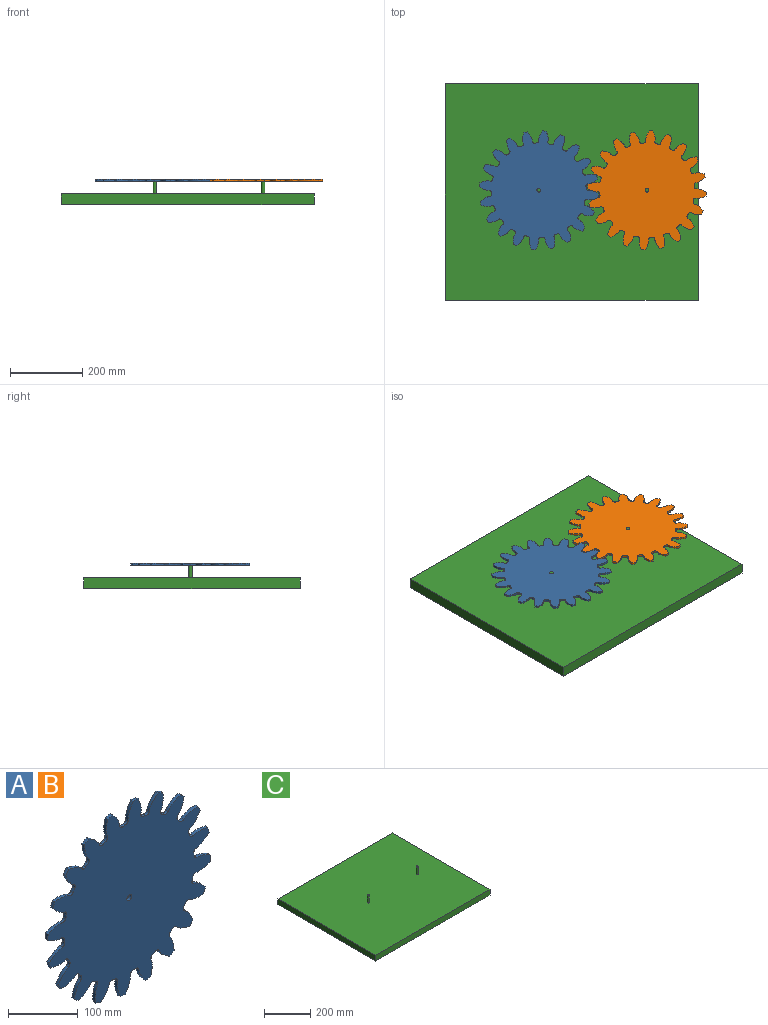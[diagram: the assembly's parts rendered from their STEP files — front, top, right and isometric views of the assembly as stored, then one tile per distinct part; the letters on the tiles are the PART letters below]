
ASSEMBLY  parts=3 mates=2
PART A: 123 faces, bbox 329.9x5.1x329.9 mm
  f0: extruded ~29.78x5.08mm, area 154.3mm2, adj f80,f81,f82,f83
  f1: cylinder r=131.25mm len=5.54mm, axis (0,1,0), area 30.4mm2, adj f81,f82,f83,f84
  f2: extruded ~21.5x20.61mm, area 154.3mm2, adj f3,f81,f82,f84
  f3: cylinder r=165mm len=8.88mm, axis (0,1,0), area 52.9mm2, adj f2,f4,f81,f82
  f4: extruded ~28.52x8.6mm, area 154.3mm2, adj f3,f81,f82,f85
  f5: cylinder r=131.25mm len=5.08mm, axis (0,1,0), area 30.4mm2, adj f81,f82,f85,f86
  f6: extruded ~26.82x12.95mm, area 154.3mm2, adj f7,f81,f82,f86
  f7: cylinder r=165mm len=7.92mm, axis (0,1,0), area 52.9mm2, adj f6,f8,f81,f82
  f8: extruded ~24.46x16.99mm, area 154.3mm2, adj f7,f81,f82,f87
  f9: cylinder r=131.25mm len=5.11mm, axis (0,1,0), area 30.4mm2, adj f81,f82,f87,f88
  f10: extruded ~29.51x5.08mm, area 154.3mm2, adj f11,f81,f82,f88
  f11: cylinder r=165mm len=9.62mm, axis (0,1,0), area 52.9mm2, adj f10,f12,f81,f82
  f12: extruded ~23.72x18.01mm, area 154.3mm2, adj f11,f81,f82,f89
  f13: cylinder r=131.25mm len=5.83mm, axis (0,1,0), area 30.4mm2, adj f81,f82,f89,f90
  f14: extruded ~29.31x6.11mm, area 154.3mm2, adj f15,f81,f82,f90
  f15: cylinder r=165mm len=10.38mm, axis (0,1,0), area 52.9mm2, adj f14,f16,f81,f82
  f16: extruded ~28.12x9.85mm, area 154.3mm2, adj f15,f81,f82,f91
  f17: cylinder r=131.25mm len=5.97mm, axis (0,1,0), area 30.4mm2, adj f81,f82,f91,f92
  f18: extruded ~26.24x14.08mm, area 154.3mm2, adj f19,f81,f82,f92
  f19: cylinder r=165mm len=10.13mm, axis (0,1,0), area 52.9mm2, adj f18,f20,f81,f82
  f20: extruded ~29.78x5.08mm, area 154.3mm2, adj f19,f81,f82,f93
  f21: cylinder r=131.25mm len=5.54mm, axis (0,1,0), area 30.4mm2, adj f81,f82,f93,f94
  f22: extruded ~21.5x20.61mm, area 154.3mm2, adj f23,f81,f82,f94
  f23: cylinder r=165mm len=8.88mm, axis (0,1,0), area 52.9mm2, adj f22,f24,f81,f82
  f24: extruded ~28.52x8.6mm, area 154.3mm2, adj f23,f81,f82,f95
  f25: cylinder r=131.25mm len=5.08mm, axis (0,1,0), area 30.4mm2, adj f81,f82,f95,f96
  f26: extruded ~26.82x12.95mm, area 154.3mm2, adj f27,f81,f82,f96
  f27: cylinder r=165mm len=7.92mm, axis (0,1,0), area 52.9mm2, adj f26,f28,f81,f82
  f28: extruded ~24.46x16.99mm, area 154.3mm2, adj f27,f81,f82,f97
  f29: cylinder r=131.25mm len=5.11mm, axis (0,1,0), area 30.4mm2, adj f81,f82,f97,f98
  f30: extruded ~29.51x5.08mm, area 154.3mm2, adj f31,f81,f82,f98
  f31: cylinder r=165mm len=9.62mm, axis (0,1,0), area 52.9mm2, adj f30,f32,f81,f82
  f32: extruded ~23.72x18.01mm, area 154.3mm2, adj f31,f81,f82,f99
  f33: cylinder r=131.25mm len=5.83mm, axis (0,1,0), area 30.4mm2, adj f81,f82,f99,f100
  f34: extruded ~29.31x6.11mm, area 154.3mm2, adj f35,f81,f82,f100
  f35: cylinder r=165mm len=10.38mm, axis (0,1,0), area 52.9mm2, adj f34,f36,f81,f82
  f36: extruded ~28.12x9.85mm, area 154.3mm2, adj f35,f81,f82,f101
  f37: cylinder r=131.25mm len=5.97mm, axis (0,1,0), area 30.4mm2, adj f81,f82,f101,f102
  f38: extruded ~26.24x14.08mm, area 154.3mm2, adj f39,f81,f82,f102
  f39: cylinder r=165mm len=10.13mm, axis (0,1,0), area 52.9mm2, adj f38,f40,f81,f82
  f40: extruded ~29.78x5.08mm, area 154.3mm2, adj f39,f81,f82,f103
  f41: cylinder r=131.25mm len=5.54mm, axis (0,1,0), area 30.4mm2, adj f81,f82,f103,f104
  f42: extruded ~21.5x20.61mm, area 154.3mm2, adj f43,f81,f82,f104
  f43: cylinder r=165mm len=8.88mm, axis (0,1,0), area 52.9mm2, adj f42,f44,f81,f82
  f44: extruded ~28.52x8.6mm, area 154.3mm2, adj f43,f81,f82,f105
  f45: cylinder r=131.25mm len=5.08mm, axis (0,1,0), area 30.4mm2, adj f81,f82,f105,f106
  f46: extruded ~26.82x12.95mm, area 154.3mm2, adj f47,f81,f82,f106
  f47: cylinder r=165mm len=7.92mm, axis (0,1,0), area 52.9mm2, adj f46,f48,f81,f82
  f48: extruded ~24.46x16.99mm, area 154.3mm2, adj f47,f81,f82,f107
  f49: cylinder r=131.25mm len=5.11mm, axis (0,1,0), area 30.4mm2, adj f81,f82,f107,f108
  f50: extruded ~29.51x5.08mm, area 154.3mm2, adj f51,f81,f82,f108
  f51: cylinder r=165mm len=9.62mm, axis (0,1,0), area 52.9mm2, adj f50,f52,f81,f82
  f52: extruded ~23.72x18.01mm, area 154.3mm2, adj f51,f81,f82,f109
  f53: cylinder r=131.25mm len=5.83mm, axis (0,1,0), area 30.4mm2, adj f81,f82,f109,f110
  f54: extruded ~29.31x6.11mm, area 154.3mm2, adj f55,f81,f82,f110
  f55: cylinder r=165mm len=10.38mm, axis (0,1,0), area 52.9mm2, adj f54,f56,f81,f82
  f56: extruded ~28.12x9.85mm, area 154.3mm2, adj f55,f81,f82,f111
  f57: cylinder r=131.25mm len=5.97mm, axis (0,1,0), area 30.4mm2, adj f81,f82,f111,f112
  f58: extruded ~26.24x14.08mm, area 154.3mm2, adj f59,f81,f82,f112
  f59: cylinder r=165mm len=10.13mm, axis (0,1,0), area 52.9mm2, adj f58,f60,f81,f82
  f60: extruded ~29.78x5.08mm, area 154.3mm2, adj f59,f81,f82,f113
  f61: cylinder r=131.25mm len=5.54mm, axis (0,1,0), area 30.4mm2, adj f81,f82,f113,f114
  f62: extruded ~21.5x20.61mm, area 154.3mm2, adj f63,f81,f82,f114
  f63: cylinder r=165mm len=8.88mm, axis (0,1,0), area 52.9mm2, adj f62,f64,f81,f82
  f64: extruded ~28.52x8.6mm, area 154.3mm2, adj f63,f81,f82,f115
  f65: cylinder r=131.25mm len=5.08mm, axis (0,1,0), area 30.4mm2, adj f81,f82,f115,f116
  f66: extruded ~26.82x12.95mm, area 154.3mm2, adj f67,f81,f82,f116
  f67: cylinder r=165mm len=7.92mm, axis (0,1,0), area 52.9mm2, adj f66,f68,f81,f82
  f68: extruded ~24.46x16.99mm, area 154.3mm2, adj f67,f81,f82,f117
  f69: cylinder r=131.25mm len=5.11mm, axis (0,1,0), area 30.4mm2, adj f81,f82,f117,f118
  f70: extruded ~29.51x5.08mm, area 154.3mm2, adj f71,f81,f82,f118
  f71: cylinder r=165mm len=9.62mm, axis (0,1,0), area 52.9mm2, adj f70,f72,f81,f82
  f72: extruded ~23.72x18.01mm, area 154.3mm2, adj f71,f81,f82,f119
  f73: cylinder r=131.25mm len=5.83mm, axis (0,1,0), area 30.4mm2, adj f81,f82,f119,f120
  f74: extruded ~29.31x6.11mm, area 154.3mm2, adj f75,f81,f82,f120
  f75: cylinder r=165mm len=10.38mm, axis (0,1,0), area 52.9mm2, adj f74,f76,f81,f82
  f76: extruded ~28.12x9.85mm, area 154.3mm2, adj f75,f81,f82,f121
  f77: cylinder r=131.25mm len=5.97mm, axis (0,1,0), area 30.4mm2, adj f81,f82,f121,f122
  f78: extruded ~26.24x14.08mm, area 154.3mm2, adj f80,f81,f82,f122
  f79: cylinder r=5mm len=10mm, axis (0,1,0), area 159.6mm2, adj f81,f82
  f80: cylinder r=165mm len=10.13mm, axis (0,1,0), area 52.9mm2, adj f0,f78,f81,f82
  f81: plane 329.87x329.87mm, normal (0,-1,0), area 69145.6mm2, adj f0,f1,f2,f3,f4,f5,f6,f7
  f82: plane 329.87x329.87mm, normal (0,1,0), area 69145.6mm2, adj f0,f1,f2,f3,f4,f5,f6,f7
  f83: cylinder r=5.56mm len=6.99mm, axis (0,1,0), area 43.3mm2, adj f0,f1,f81,f82
  f84: cylinder r=5.56mm len=7.25mm, axis (0,1,0), area 43.3mm2, adj f1,f2,f81,f82
  f85: cylinder r=5.56mm len=7.66mm, axis (0,1,0), area 43.3mm2, adj f4,f5,f81,f82
  f86: cylinder r=5.56mm len=7.71mm, axis (0,1,0), area 43.3mm2, adj f5,f6,f81,f82
  f87: cylinder r=5.56mm len=7.57mm, axis (0,1,0), area 43.3mm2, adj f8,f9,f81,f82
  f88: cylinder r=5.56mm len=7.42mm, axis (0,1,0), area 43.3mm2, adj f9,f10,f81,f82
  f89: cylinder r=5.56mm len=6.74mm, axis (0,1,0), area 43.3mm2, adj f12,f13,f81,f82
  f90: cylinder r=5.56mm len=6.4mm, axis (0,1,0), area 43.3mm2, adj f13,f14,f81,f82
  f91: cylinder r=5.56mm len=5.65mm, axis (0,1,0), area 43.3mm2, adj f16,f17,f81,f82
  f92: cylinder r=5.56mm len=6.07mm, axis (0,1,0), area 43.3mm2, adj f17,f18,f81,f82
  f93: cylinder r=5.56mm len=6.99mm, axis (0,1,0), area 43.3mm2, adj f20,f21,f81,f82
  f94: cylinder r=5.56mm len=7.25mm, axis (0,1,0), area 43.3mm2, adj f21,f22,f81,f82
  f95: cylinder r=5.56mm len=7.66mm, axis (0,1,0), area 43.3mm2, adj f24,f25,f81,f82
  f96: cylinder r=5.56mm len=7.71mm, axis (0,1,0), area 43.3mm2, adj f25,f26,f81,f82
  f97: cylinder r=5.56mm len=7.57mm, axis (0,1,0), area 43.3mm2, adj f28,f29,f81,f82
  f98: cylinder r=5.56mm len=7.42mm, axis (0,1,0), area 43.3mm2, adj f29,f30,f81,f82
  f99: cylinder r=5.56mm len=6.74mm, axis (0,1,0), area 43.3mm2, adj f32,f33,f81,f82
  f100: cylinder r=5.56mm len=6.4mm, axis (0,1,0), area 43.3mm2, adj f33,f34,f81,f82
  f101: cylinder r=5.56mm len=5.65mm, axis (0,1,0), area 43.3mm2, adj f36,f37,f81,f82
  f102: cylinder r=5.56mm len=6.07mm, axis (0,1,0), area 43.3mm2, adj f37,f38,f81,f82
  f103: cylinder r=5.56mm len=6.99mm, axis (0,1,0), area 43.3mm2, adj f40,f41,f81,f82
  f104: cylinder r=5.56mm len=7.25mm, axis (0,1,0), area 43.3mm2, adj f41,f42,f81,f82
  f105: cylinder r=5.56mm len=7.66mm, axis (0,1,0), area 43.3mm2, adj f44,f45,f81,f82
  f106: cylinder r=5.56mm len=7.71mm, axis (0,1,0), area 43.3mm2, adj f45,f46,f81,f82
  f107: cylinder r=5.56mm len=7.57mm, axis (0,1,0), area 43.3mm2, adj f48,f49,f81,f82
  f108: cylinder r=5.56mm len=7.42mm, axis (0,1,0), area 43.3mm2, adj f49,f50,f81,f82
  f109: cylinder r=5.56mm len=6.74mm, axis (0,1,0), area 43.3mm2, adj f52,f53,f81,f82
  f110: cylinder r=5.56mm len=6.4mm, axis (0,1,0), area 43.3mm2, adj f53,f54,f81,f82
  f111: cylinder r=5.56mm len=5.65mm, axis (0,1,0), area 43.3mm2, adj f56,f57,f81,f82
  f112: cylinder r=5.56mm len=6.07mm, axis (0,1,0), area 43.3mm2, adj f57,f58,f81,f82
  f113: cylinder r=5.56mm len=6.99mm, axis (0,1,0), area 43.3mm2, adj f60,f61,f81,f82
  f114: cylinder r=5.56mm len=7.25mm, axis (0,1,0), area 43.3mm2, adj f61,f62,f81,f82
  f115: cylinder r=5.56mm len=7.66mm, axis (0,1,0), area 43.3mm2, adj f64,f65,f81,f82
  f116: cylinder r=5.56mm len=7.71mm, axis (0,1,0), area 43.3mm2, adj f65,f66,f81,f82
  f117: cylinder r=5.56mm len=7.57mm, axis (0,1,0), area 43.3mm2, adj f68,f69,f81,f82
  f118: cylinder r=5.56mm len=7.42mm, axis (0,1,0), area 43.3mm2, adj f69,f70,f81,f82
  f119: cylinder r=5.56mm len=6.74mm, axis (0,1,0), area 43.3mm2, adj f72,f73,f81,f82
  f120: cylinder r=5.56mm len=6.4mm, axis (0,1,0), area 43.3mm2, adj f73,f74,f81,f82
  f121: cylinder r=5.56mm len=5.65mm, axis (0,1,0), area 43.3mm2, adj f76,f77,f81,f82
  f122: cylinder r=5.56mm len=6.07mm, axis (0,1,0), area 43.3mm2, adj f77,f78,f81,f82
PART B: same geometry as A
PART C: 10 faces, bbox 700x600x70 mm
  f0: plane 600x30mm, normal (-1,0,0), area 18000mm2, adj f1,f3,f4,f5
  f1: plane 700x30mm, normal (0,-1,0), area 21000mm2, adj f0,f2,f4,f5
  f2: plane 600x30mm, normal (1,0,0), area 18000mm2, adj f1,f3,f4,f5
  f3: plane 700x30mm, normal (0,1,0), area 21000mm2, adj f0,f2,f4,f5
  f4: plane 700x600mm, normal (0,0,1), area 419842.9mm2, adj f0,f1,f2,f3,f6,f8
  f5: plane 700x600mm, normal (0,0,-1), area 420000mm2, adj f0,f1,f2,f3
  f6: cylinder r=5mm len=40mm, axis (0,0,-1), area 1256.6mm2, adj f4,f7
  f7: plane 10x10mm, normal (0,0,1), area 78.5mm2, adj f6
  f8: cylinder r=5mm len=40mm, axis (0,0,-1), area 1256.6mm2, adj f4,f9
  f9: plane 10x10mm, normal (0,0,1), area 78.5mm2, adj f8
PLACE A rot(axis=(-0.11,0.7,-0.7),167.8deg) t=(-141.91,-18.32,39.24)mm
PLACE B rot(axis=(-0.11,-0.7,0.7),167.8deg) t=(158.09,-18.32,39.24)mm
PLACE C t=(-45.28,-81.43,-25.68)mm fixed
MATE revolute B.f3 <-> C.f8  axis (0,0,1) through (158.09,-18.32,44.32)mm
MATE revolute A.f3 <-> C.f6  axis (0,0,1) through (-141.91,-18.32,44.32)mm
